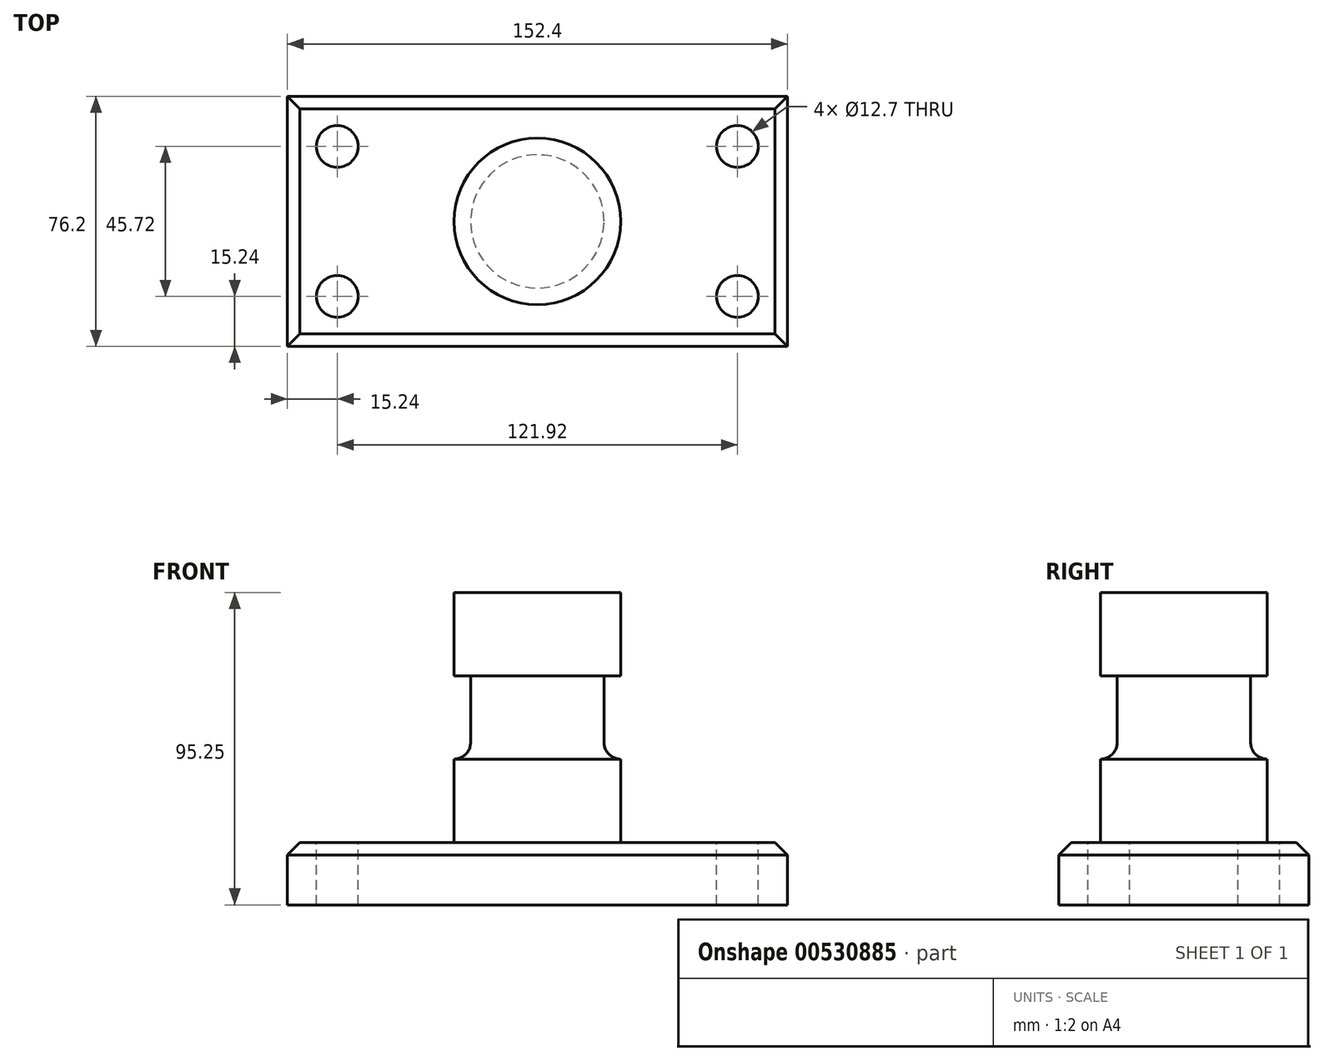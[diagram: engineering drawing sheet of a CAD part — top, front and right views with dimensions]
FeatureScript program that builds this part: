
annotation { "Feature Type Name" : "Feature", "Feature Type Description" : "" }
export const myFeature = defineFeature(function(context is Context, id is Id, definition is map)
    precondition{}
    {
        {
            var Q0;
            Q0=qCreatedBy(makeId("Top.planeOp"),FACE);
            var sketch = newSketch(context, id + "F0", { "sketchPlane" : qUnion([Q0])});
            skLineSegment(sketch, "E0.bottom", {"start": v(76.2, 38.1) * mm, "end": v(-76.2, 38.1) * mm});
            skLineSegment(sketch, "E0.top", {"start": v(76.2, -38.1) * mm, "end": v(-76.2, -38.1) * mm});
            skLineSegment(sketch, "E0.left", {"start": v(76.2, 38.1) * mm, "end": v(76.2, -38.1) * mm});
            skLineSegment(sketch, "E0.right", {"start": v(-76.2, 38.1) * mm, "end": v(-76.2, -38.1) * mm});
            skPoint(sketch, "E0.middle", {"position": v(0, 0) * mm});
            skSolve(sketch);
        }
        {
            var Q0;
            Q0 = qSketchRegion(id + "F0", true);
            extrude(context, id + "F1", {"entities" : qUnion([Q0]), "depth" : 19.05 * mm, "offsetDistance" : 25.4 * mm});
        }
        {
            var Q0;
            Q0=makeQuery(id+"F1.opExtrude","CAP_FACE",FACE,{"disambiguationData":[OSD([sQuery(id+"F0.wireOp",EDGE,"E0.bottom"),sQuery(id+"F0.wireOp",EDGE,"E0.top"),sQuery(id+"F0.wireOp",EDGE,"E0.left"),sQuery(id+"F0.wireOp",EDGE,"E0.right")])],"isStart":false});
            var sketch = newSketch(context, id + "F2", { "sketchPlane" : qUnion([Q0])});
            skCircle(sketch, "E1", {"center": v(-60.96, 22.86) * mm, "radius": 6.35 * mm});
            skCircle(sketch, "E2.MirrorC", {"center": v(-60.96, -22.86) * mm, "radius": 6.35 * mm});
            skCircle(sketch, "E3.MirrorC", {"center": v(60.96, 22.86) * mm, "radius": 6.35 * mm});
            skCircle(sketch, "E4.MirrorC", {"center": v(60.96, -22.86) * mm, "radius": 6.35 * mm});
            skSolve(sketch);
        }
        {
            var Q0;
            Q0 = qSketchRegion(id + "F2", true);
            var Q1;
            Q1=makeQuery(id+"F1.opExtrude","CAP_FACE",FACE,{"disambiguationData":[OSD([sQuery(id+"F0.wireOp",EDGE,"E0.bottom"),sQuery(id+"F0.wireOp",EDGE,"E0.top"),sQuery(id+"F0.wireOp",EDGE,"E0.left"),sQuery(id+"F0.wireOp",EDGE,"E0.right")])],"isStart":true});
            extrude(context, id + "F3", {"entities" : qUnion([Q0]), "operationType" : NewBodyOperationType.REMOVE, "endBound" : BoundingType.UP_TO_SURFACE, "oppositeDirection" : true, "depth" : 25.4 * mm, "endBoundEntityFace" : qUnion([Q1]), "offsetDistance" : 25.4 * mm});
        }
        {
            var Q0;
            Q0=makeQuery(id+"F1.opExtrude","CAP_EDGE",EDGE,{"disambiguationData":[OSD([sQuery(id+"F0.wireOp",EDGE,"E0.top")])],"isStart":false});
            var Q1;
            Q1=makeQuery(id+"F1.opExtrude","CAP_EDGE",EDGE,{"disambiguationData":[OSD([sQuery(id+"F0.wireOp",EDGE,"E0.left")])],"isStart":false});
            var Q2;
            Q2=makeQuery(id+"F1.opExtrude","CAP_EDGE",EDGE,{"disambiguationData":[OSD([sQuery(id+"F0.wireOp",EDGE,"E0.bottom")])],"isStart":false});
            var Q3;
            Q3=makeQuery(id+"F1.opExtrude","CAP_EDGE",EDGE,{"disambiguationData":[OSD([sQuery(id+"F0.wireOp",EDGE,"E0.right")])],"isStart":false});
            chamfer(context, id + "F4", {"entities" : qUnion([Q0, Q1, Q2, Q3]), "width" : 3.8 * mm, "tangentPropagation" : true});
        }
        {
            var Q0;
            Q0=qCreatedBy(makeId("Front.planeOp"),FACE);
            var sketch = newSketch(context, id + "F5", { "sketchPlane" : qUnion([Q0])});
            skLineSegment(sketch, "E5.bottom", {"start": v(0, 19.05) * mm, "end": v(25.4, 19.05) * mm});
            skLineSegment(sketch, "E5.top", {"start": v(0, 69.85) * mm, "end": v(20.32, 69.85) * mm});
            skLineSegment(sketch, "E5.left", {"start": v(0, 19.05) * mm, "end": v(0, 69.85) * mm});
            skLineSegment(sketch, "E5.right", {"start": v(25.4, 19.05) * mm, "end": v(25.4, 44.45) * mm});
            skLineSegment(sketch, "E6", {"start": v(20.32, 69.85) * mm, "end": v(20.32, 44.45) * mm});
            skLineSegment(sketch, "E7", {"start": v(20.32, 44.45) * mm, "end": v(25.4, 44.45) * mm});
            skSolve(sketch);
        }
        {
            var Q0;
            Q0 = qSketchRegion(id + "F5", true);
            var Q1;
            Q1=sQuery(id+"F5.wireOp",EDGE,"E5.left");
            revolve(context, id + "F6", {"operationType" : NewBodyOperationType.ADD, "entities" : qUnion([Q0]), "axis" : qUnion([Q1]), "revolveType" : RevolveType.FULL});
        }
        {
            var Q0;
            Q0=makeQuery(id+"F6.opRevolve","SWEPT_FACE",FACE,{"disambiguationData":[OSD([sQuery(id+"F5.wireOp",EDGE,"E5.top")])]});
            var sketch = newSketch(context, id + "F7", { "sketchPlane" : qUnion([Q0])});
            skCircle(sketch, "E8", {"center": v(0, 0) * mm, "radius": 25.4 * mm});
            skSolve(sketch);
        }
        {
            var Q0;
            Q0 = qSketchRegion(id + "F7", true);
            extrude(context, id + "F8", {"entities" : qUnion([Q0]), "operationType" : NewBodyOperationType.ADD, "depth" : 25.4 * mm, "offsetDistance" : 25.4 * mm});
        }
        {
            var Q0;
            Q0=makeQuery(id+"F6.opRevolve","SWEPT_EDGE",EDGE,{"disambiguationData":[OSD([sQuery(id+"F5.wireOp",EDGE,"E5.bottom"),sQuery(id+"F5.wireOp",EDGE,"E5.right")])]});
            var Q1;
            Q1=makeQuery(id+"F6.opRevolve","SWEPT_EDGE",EDGE,{"disambiguationData":[OSD([sQuery(id+"F5.wireOp",EDGE,"E6"),sQuery(id+"F5.wireOp",EDGE,"E7")])]});
            var Q2;
            Q2=makeQuery(id+"F6.opRevolve","SWEPT_EDGE",EDGE,{"disambiguationData":[OSD([sQuery(id+"F5.wireOp",EDGE,"E5.top"),sQuery(id+"F5.wireOp",EDGE,"E6")])]});
            fillet(context, id + "F9", {"entities" : qUnion([Q0, Q1, Q2]), "radius" : 5.08 * mm, "tangentPropagation" : true, "allowEdgeOverflow" : false});
        }
    });
